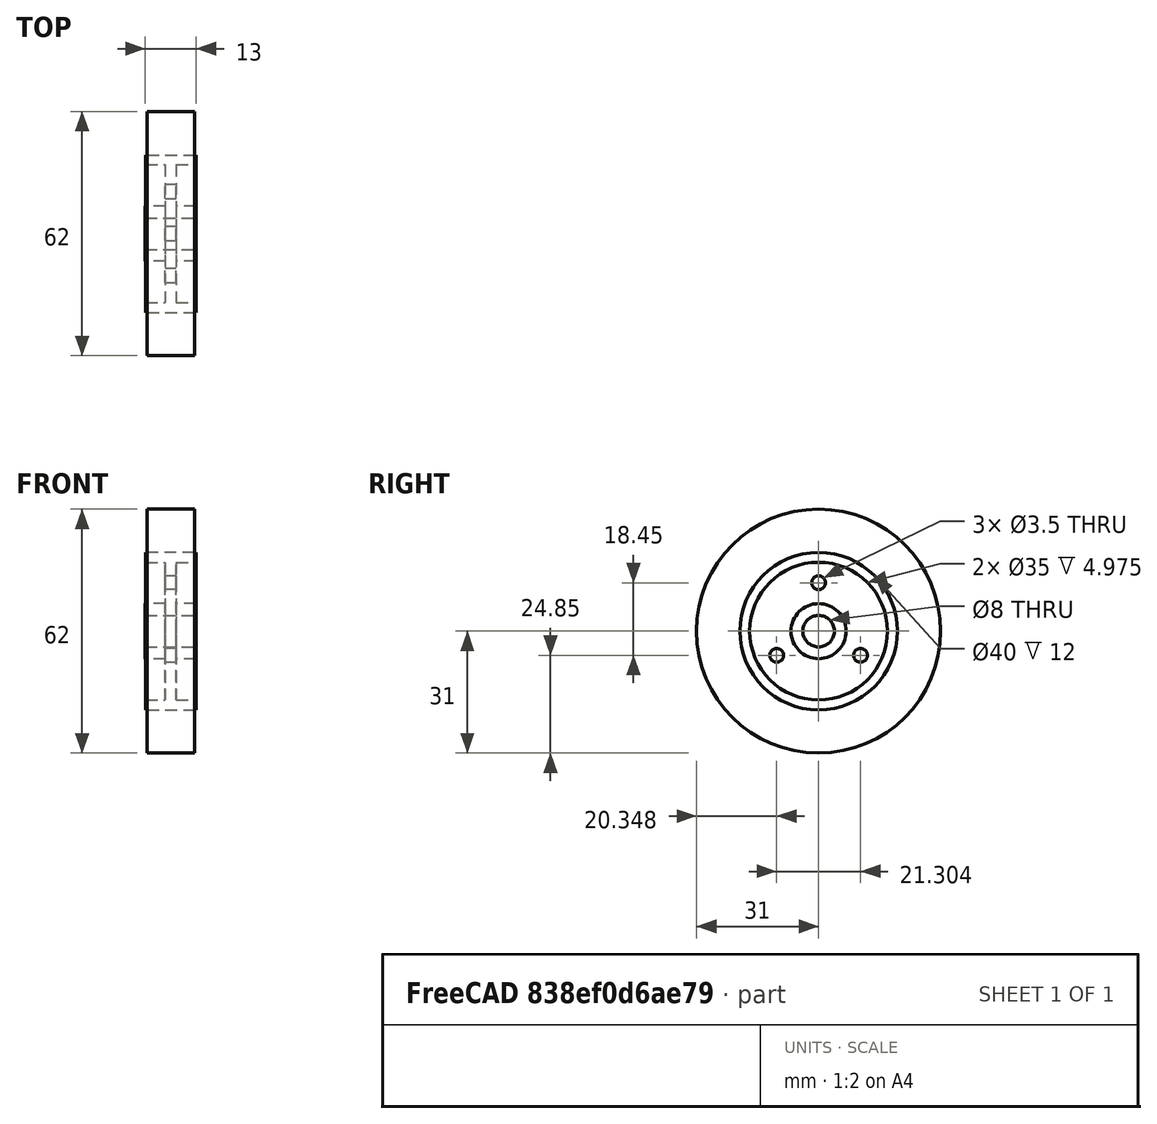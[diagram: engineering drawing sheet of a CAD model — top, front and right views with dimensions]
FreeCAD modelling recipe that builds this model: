
FCSTD DOCUMENT  (FreeCAD 0.17R13541 (Git))
Label: HP600_wheel
License: All rights reserved
LicenseURL: http://en.wikipedia.org/wiki/All_rights_reserved
objects: App::FeaturePython×4, Part::FeaturePython×2, PartDesign::FeatureBase×1, PartDesign::Body×1
note: 4 computed .brp shape members not serialized (recipe doc carries the construction recipe); baked Part::Feature solids carry a one-line shape summary decoded from their .brp

FEATURE [Part::FeaturePython] HP600_wheel_hub_01  # a2plus imported part (geometry in sourceFile) (typed FeaturePython)
  fixedPosition = true
  sourceFile = <userpath>/Projects/minirobots/HP600_wheel-hub.fcstd
  timeLastImport = 1.542e+09
  updateColors = true
FEATURE [Part::FeaturePython] HP600_wheel_rubber_01  # a2plus imported part (geometry in sourceFile) (typed FeaturePython)
  Placement = pos=(0,0,0) rot=(0,-1,0;1.5708rad)
  fixedPosition = false
  sourceFile = <userpath>/Projects/minirobots/HP600_wheel-rubber.fcstd
  timeLastImport = 1.54193e+09
  updateColors = true
FEATURE [App::FeaturePython] axialConstraint01  label="axialConstraint01__HP600_wheel_hub_01"  # a2plus constraint (typed FeaturePython)
  Object1 = HP600_wheel_rubber_01
  Object2 = HP600_wheel_hub_01
  SubElement1 = Face2
  SubElement2 = Face2
  Type = axial
  directionConstraint = 0
  lockRotation = false
FEATURE [App::FeaturePython] axialConstraint01_mirror  label="axialConstraint01__HP600_wheel_rubber_01"  # a2plus constraint (typed FeaturePython)
  Object1 = HP600_wheel_rubber_01
  Object2 = HP600_wheel_hub_01
  SubElement1 = Face2
  SubElement2 = Face2
  Type = axial
  directionConstraint = 0
  lockRotation = false
FEATURE [App::FeaturePython] planeConstraint01  label="planeConstraint01__HP600_wheel_hub_01"  # a2plus constraint (typed FeaturePython)
  Object1 = HP600_wheel_rubber_01
  Object2 = HP600_wheel_hub_01
  SubElement1 = Face3
  SubElement2 = Face4
  Type = plane
  directionConstraint = 0
  offset = 0.375
FEATURE [App::FeaturePython] planeConstraint01_mirror  label="planeConstraint01__HP600_wheel_rubber_01"  # a2plus constraint (typed FeaturePython)
  Object1 = HP600_wheel_rubber_01
  Object2 = HP600_wheel_hub_01
  SubElement1 = Face3
  SubElement2 = Face4
  Type = plane
  directionConstraint = 0
  offset = 0.375
FEATURE [PartDesign::FeatureBase] BaseFeature
  BaseFeature = -> HP600_wheel_hub_01
FEATURE [PartDesign::Body] Body
  BaseFeature = -> HP600_wheel_hub_01
  Group = -> [BaseFeature]
  Origin = -> Origin
  Tip = -> BaseFeature
